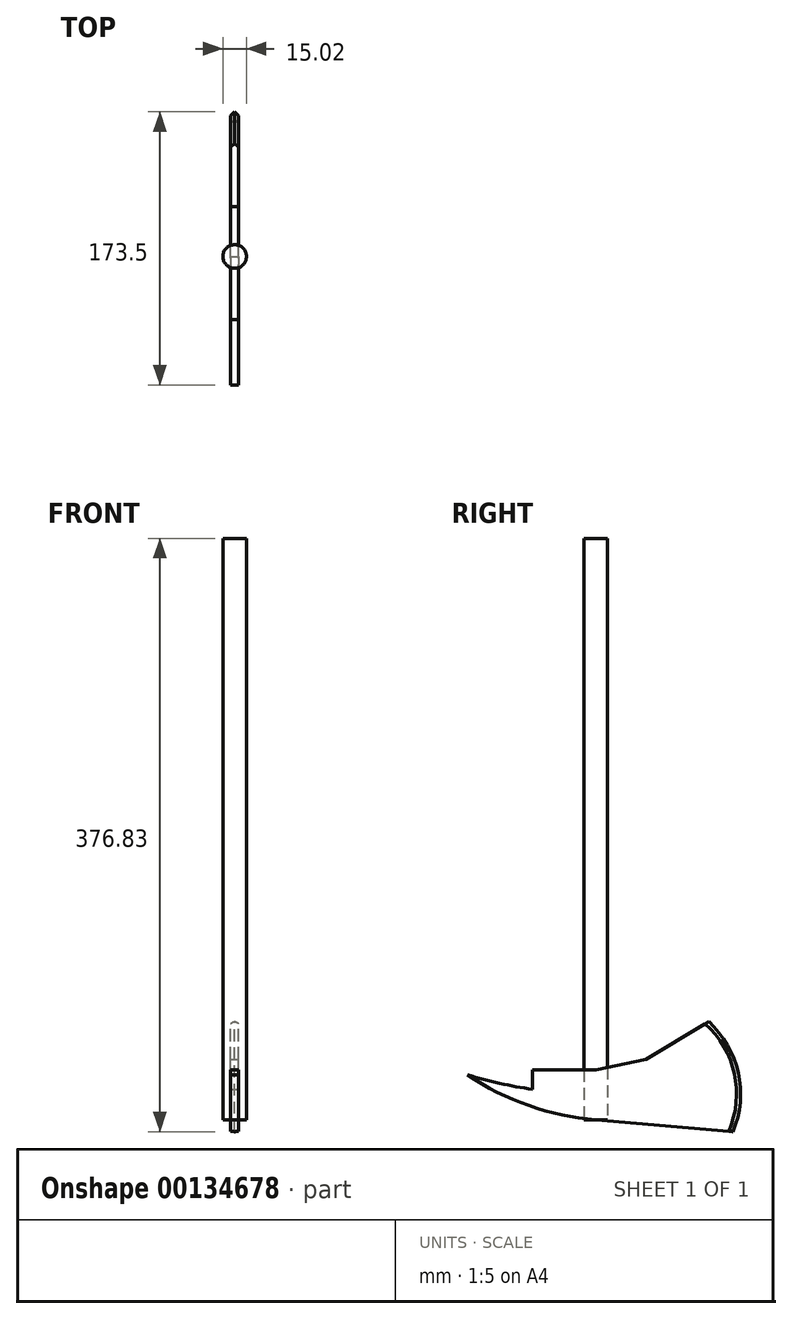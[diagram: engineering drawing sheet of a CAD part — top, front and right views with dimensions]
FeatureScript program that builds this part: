
annotation { "Feature Type Name" : "Feature", "Feature Type Description" : "" }
export const myFeature = defineFeature(function(context is Context, id is Id, definition is map)
    precondition{}
    {
        {
            var Q0;
            Q0=qCreatedBy(makeId("Top.planeOp"),FACE);
            var sketch = newSketch(context, id + "F0", { "sketchPlane" : qUnion([Q0])});
            skCircle(sketch, "E0", {"center": v(0, 0) * mm, "radius": 7.51 * mm});
            skSolve(sketch);
        }
        {
            var Q0;
            Q0 = qSketchRegion(id + "F0", true);
            extrude(context, id + "F1", {"entities" : qUnion([Q0]), "depth" : 369.42 * mm});
        }
        {
            var Q0;
            Q0=qCreatedBy(makeId("Right.planeOp"),FACE);
            var sketch = newSketch(context, id + "F2", { "sketchPlane" : qUnion([Q0])});
            skLineSegment(sketch, "E1", {"start": v(0, 0) * mm, "end": v(87.1, -7.41) * mm});
            skArc(sketch, "E2", {"start": v(87.1, -7.41) * mm, "mid": v(90.48, 30) * mm, "end": v(71.67, 62.51) * mm});
            skLineSegment(sketch, "E3", {"start": v(0, 19.42) * mm, "end": v(0, 0) * mm});
            skLineSegment(sketch, "E4", {"start": v(0, 19.42) * mm, "end": v(71.67, 62.51) * mm});
            skLineSegment(sketch, "E5", {"start": v(0, 19.42) * mm, "end": v(0, 31.76) * mm});
            skLineSegment(sketch, "E6", {"start": v(0, 31.76) * mm, "end": v(-23.74, 31.76) * mm});
            skLineSegment(sketch, "E7", {"start": v(-23.74, 31.76) * mm, "end": v(-40.15, 31.76) * mm});
            skLineSegment(sketch, "E8", {"start": v(-40.15, 19.42) * mm, "end": v(0, 19.42) * mm});
            skLineSegment(sketch, "E9", {"start": v(-40.15, 31.76) * mm, "end": v(-40.15, 19.42) * mm});
            skArc(sketch, "E10", {"start": v(-81.57, 28.7) * mm, "mid": v(-42.62, 9.16) * mm, "end": v(0, 0) * mm});
            skArc(sketch, "E11", {"start": v(-81.57, 28.7) * mm, "mid": v(-61.04, 23.29) * mm, "end": v(-40.15, 19.42) * mm});
            skLineSegment(sketch, "E12", {"start": v(0, 31.76) * mm, "end": v(31.69, 38.47) * mm});
            skSolve(sketch);
        }
        {
            var Q0;
            Q0=makeQuery(id+"F2.imprint","IMPRINT",FACE,{"disambiguationData":[TD([[makeQuery(id+"F2.imprint","IMPRINT",EDGE,{"derivedFrom":sQuery(id+"F2.wireOp",EDGE,"E1")}),1.0]])]});
            var Q1;
            Q1=makeQuery(id+"F2.imprint","IMPRINT",FACE,{"disambiguationData":[TD([[makeQuery(id+"F2.imprint","IMPRINT",EDGE,{"derivedFrom":sQuery(id+"F2.wireOp",EDGE,"E3")}),-1.0]])]});
            var Q2;
            {var subQ3=sQuery(id+"F2.wireOp",EDGE,"E3");Q2=makeQuery(id+"F2.imprint","IMPRINT",FACE,{"disambiguationData":[TD([[makeQuery(id+"F2.imprint","IMPRINT",EDGE,{"derivedFrom":subQ3}),1.0]])]});}
            var Q3;
            {var subQ0=sQuery(id+"F2.wireOp",EDGE,"E5");Q3=makeQuery(id+"F2.imprint","IMPRINT",FACE,{"disambiguationData":[TD([[makeQuery(id+"F2.imprint","IMPRINT",EDGE,{"derivedFrom":subQ0}),-1.0]])]});}
            var Q4;
            Q4=makeQuery(id+"F2.imprint","IMPRINT",FACE,{"disambiguationData":[TD([[makeQuery(id+"F2.imprint","IMPRINT",EDGE,{"derivedFrom":sQuery(id+"F2.wireOp",EDGE,"E5")}),1.0]])]});
            extrude(context, id + "F3", {"entities" : qUnion([Q0, Q1, Q2, Q3, Q4]), "oppositeDirection" : true, "depth" : 2.54 * mm, "hasSecondDirection" : true, "secondDirectionOppositeDirection" : false, "secondDirectionDepth" : 2.54 * mm});
        }
        {
            var Q0;
            Q0=makeQuery(id+"F3.opExtrude","CAP_EDGE",EDGE,{"disambiguationData":[OSD([sQuery(id+"F2.wireOp",EDGE,"E2")])],"isStart":false});
            var Q1;
            Q1=makeQuery(id+"F3.opExtrude","CAP_EDGE",EDGE,{"disambiguationData":[OSD([sQuery(id+"F2.wireOp",EDGE,"E2")])],"isStart":true});
            chamfer(context, id + "F4", {"entities" : qUnion([Q0, Q1]), "chamferType" : ChamferType.TWO_OFFSETS, "width1" : 2.54 * mm, "oppositeDirection" : false, "width2" : 2.54 * mm, "tangentPropagation" : true});
        }
    });
